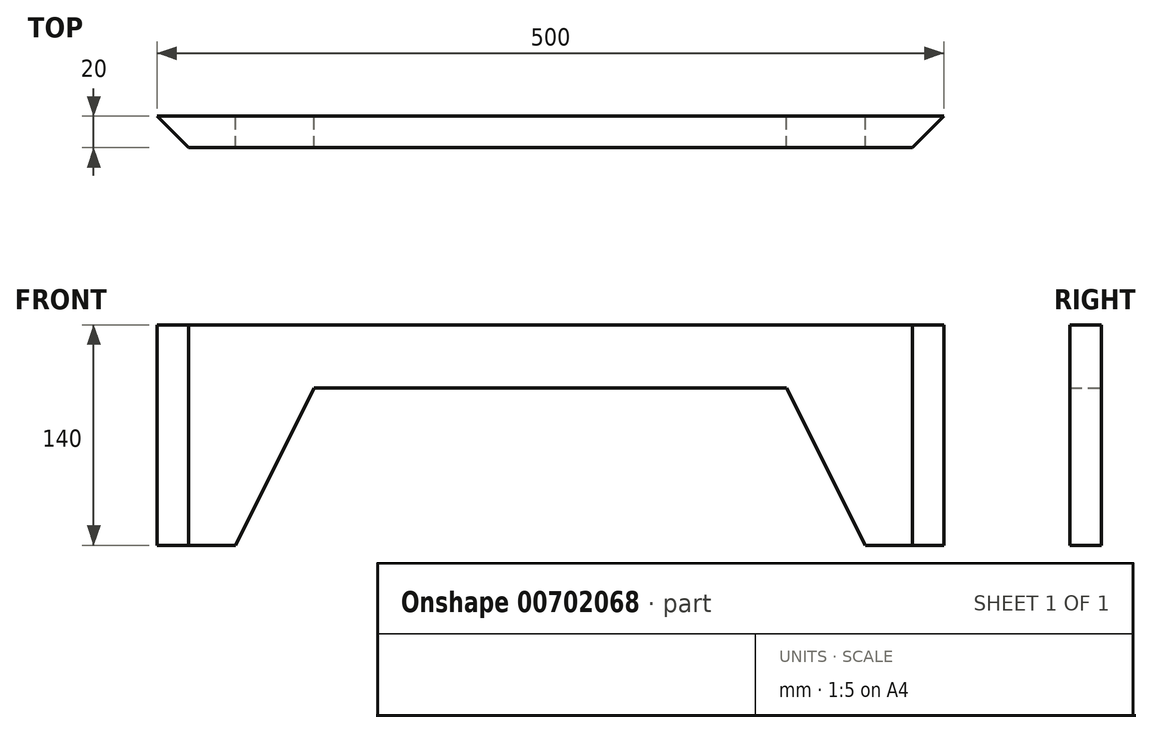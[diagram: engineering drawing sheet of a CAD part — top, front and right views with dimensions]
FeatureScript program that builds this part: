
annotation { "Feature Type Name" : "Feature", "Feature Type Description" : "" }
export const myFeature = defineFeature(function(context is Context, id is Id, definition is map)
    precondition{}
    {
        {
            var Q0;
            Q0=qCreatedBy(makeId("Front.planeOp"),FACE);
            var sketch = newSketch(context, id + "F0", { "sketchPlane" : qUnion([Q0])});
            skLineSegment(sketch, "E0.top", {"start": v(0, 140) * mm, "end": v(500, 140) * mm});
            skLineSegment(sketch, "E0.left", {"start": v(0, 0) * mm, "end": v(0, 140) * mm});
            skLineSegment(sketch, "E0.right", {"start": v(500, 0) * mm, "end": v(500, 140) * mm});
            skLineSegment(sketch, "E1", {"start": v(0, 0) * mm, "end": v(50, 0) * mm});
            skLineSegment(sketch, "E2", {"start": v(50, 0) * mm, "end": v(100, 100) * mm});
            skLineSegment(sketch, "E3", {"start": v(100, 100) * mm, "end": v(400, 100) * mm});
            skLineSegment(sketch, "E4", {"start": v(400, 100) * mm, "end": v(450, 0) * mm});
            skLineSegment(sketch, "E5", {"start": v(450, 0) * mm, "end": v(500, 0) * mm});
            skLineSegment(sketch, "E6", {"start": v(250, 140) * mm, "end": v(250, 0) * mm, "construction": true});
            skSolve(sketch);
        }
        {
            var Q0;
            Q0=qSketchRegion(id+"F0",true);
            extrude(context, id + "F1", {"entities" : qUnion([Q0]), "depth" : 20 * mm, "offsetDistance" : 25 * mm});
        }
        {
            var Q0;
            Q0=makeQuery(id+"F1.opExtrude","SWEPT_FACE",FACE,{"disambiguationData":[OSD([sQuery(id+"F0.wireOp",EDGE,"E0.top")])]});
            var sketch = newSketch(context, id + "F2", { "sketchPlane" : qUnion([Q0])});
            skLineSegment(sketch, "E7", {"start": v(0, 0) * mm, "end": v(20, -20) * mm});
            skLineSegment(sketch, "E8", {"start": v(20, -20) * mm, "end": v(480, -20) * mm});
            skLineSegment(sketch, "E9", {"start": v(480, -20) * mm, "end": v(500, 0) * mm});
            skLineSegment(sketch, "E10", {"start": v(500, 0) * mm, "end": v(500, -30) * mm});
            skLineSegment(sketch, "E11", {"start": v(500, -30) * mm, "end": v(0, -30) * mm});
            skLineSegment(sketch, "E12", {"start": v(0, -30) * mm, "end": v(0, 0) * mm});
            skSolve(sketch);
        }
        {
            var Q0;
            Q0 = qSketchRegion(id + "F2", true);
            extrude(context, id + "F3", {"entities" : qUnion([Q0]), "operationType" : NewBodyOperationType.REMOVE, "endBound" : BoundingType.THROUGH_ALL, "oppositeDirection" : true, "depth" : 25 * mm, "offsetDistance" : 25 * mm});
        }
    });
